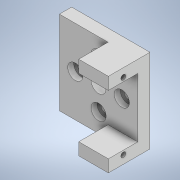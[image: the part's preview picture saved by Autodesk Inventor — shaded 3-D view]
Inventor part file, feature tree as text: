
AUTODESK INVENTOR PART (.ipt)
format: ipt  version: 2020 (Build 240168000, 168)  size: 354,304 bytes
history: native  units: in
note: dims shown in document units (in); Inventor stores cm internally (conversion verified against a paired STEP export)
features: extrude x7, sketch x7
ambient origin geometry x8: Origin, YZ Plane, XZ Plane, XY Plane, X Axis, Y Axis, Z Axis, Center Point
bodies: Solid1 (feature_tree)
feature tree (14):
  extrude  "Extrusion1"  Depth=1.2598in
  extrude  "Extrusion2"  Depth=0.1181in
  extrude  "Extrusion3"  Depth=1.5748in TaperAngle=360.0deg
  extrude  "Extrusion4"  Depth=0.1969in
  extrude  "Extrusion5"  Depth=0.0984in TaperAngle=0.0deg
  extrude  "Extrusion6"  Depth=0.1969in
  extrude  "Extrusion7"  Depth=0.4724in TaperAngle=0.0deg
  sketch  "Sketch1"  dims[d1=1.2598in d2=1.2598in]
  sketch  "Sketch2"  dims[d3=0.1969in d4=0.0in d5=0.1181in]
  sketch  "Sketch3"  dims[d6=0.374in d7=1.5748in d9=360.0deg]
  sketch  "Sketch4"  dims[d11=0.1969in d12=0.0in d13=0.2441in]
  sketch  "Sketch5"  dims[d14=1.5748in d16=360.0deg d18=0.0984in d19=0.0in]
  sketch  "Sketch8"  dims[d20=0.4764in d21=0.1969in]
  sketch  "Sketch9"  dims[d22=0.1969in d23=0.4724in d24=0.0in d25=0.2362in d26=0.3937in d27=0.0in d28=0.4764in d29=0.4764in d30=1.2598in d31=0.0433in d32=1.2598in d33=0.0433in d34=0.1969in d35=0.0in d36=0.2323in d37=0.5394in d38=0.0787in d39=0.315in d40=0.0in]
